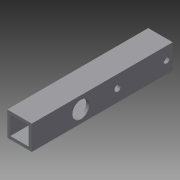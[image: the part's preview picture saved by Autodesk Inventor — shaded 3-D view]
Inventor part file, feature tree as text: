
AUTODESK INVENTOR PART (.ipt)
format: ipt  version: 2015 SP1 (Build 190203100, 203)  size: 103,936 bytes
history: native  units: in
note: dims shown in document units (in); Inventor stores cm internally (conversion verified against a paired STEP export)
features: sketch x3, hole x2, extrude x1
ambient origin geometry x8: Origin, YZ Plane, XZ Plane, XY Plane, X Axis, Y Axis, Z Axis, Center Point
bodies: Solid1 (feature_tree)
feature tree (6):
  extrude  "Extrusion1"  Depth=1.0in
  hole  "Hole1"  [1 undecoded]
  hole  "Hole2"  [1 undecoded]
  sketch  "Sketch1"  dims[d0=1.0in d1=1.0in]
  sketch  "Sketch2"  dims[d2=0.75in d3=0.75in]
  sketch  "Sketch3"  dims[d4=0.125in d5=0.125in d6=5.75in d7=0.0in d8=0.5in d9=0.25in d10=0.5in d11=2.25in d12=0.25in d13=0.75in d14=0.375in d15=0.25in d16=0.5635in d17=0.5in d18=0.8108in d19=2.0in d20=0.5in d21=0.6875in d22=0.75in d23=0.375in d24=0.25in d25=0.5635in d26=1.0in d27=0.8108in]
note: 2 required parameter values undecoded (feature->parameter linkage not recoverable at this tier; creation-order binding heuristic only, values carry confidence <= 0.55)
